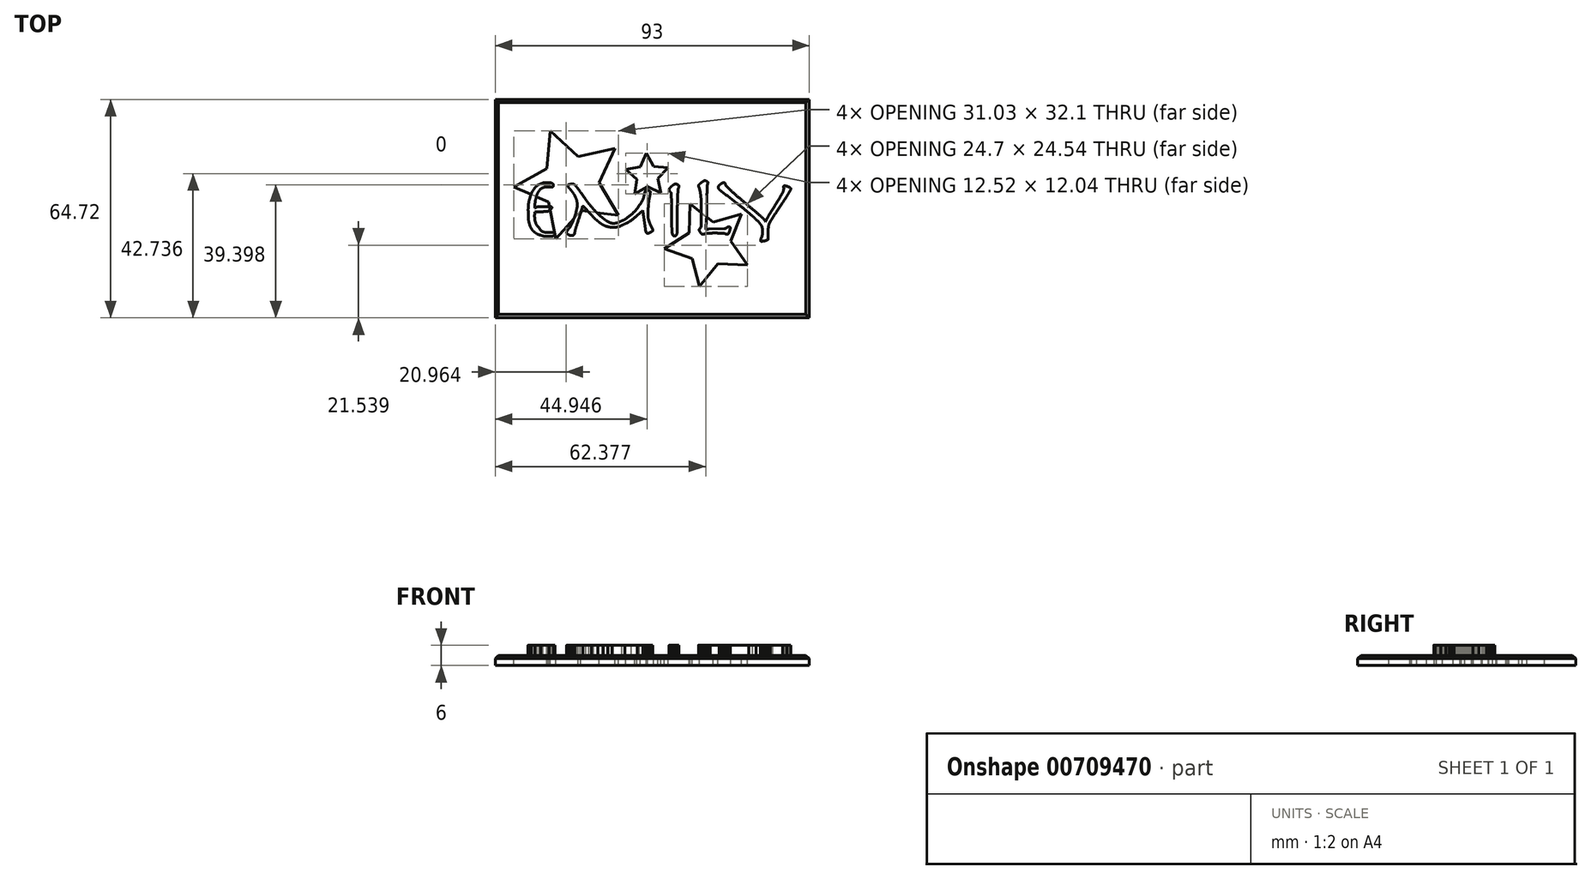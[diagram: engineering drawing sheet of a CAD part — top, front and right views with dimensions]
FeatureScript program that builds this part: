
annotation { "Feature Type Name" : "Feature", "Feature Type Description" : "" }
export const myFeature = defineFeature(function(context is Context, id is Id, definition is map)
    precondition{}
    {
        {
            var Q0;
            Q0=qCreatedBy(makeId("Top.planeOp"),FACE);
            var sketch = newSketch(context, id + "F0", { "sketchPlane" : qUnion([Q0])});
            skLineSegment(sketch, "E0", {"start": v(28.23, -16.77) * mm, "end": v(19.44, -16.28) * mm});
            skLineSegment(sketch, "E1", {"start": v(19.44, -16.28) * mm, "end": v(14.05, -23.1) * mm});
            skLineSegment(sketch, "E2", {"start": v(14.05, -23.1) * mm, "end": v(11.8, -14.75) * mm});
            skLineSegment(sketch, "E3", {"start": v(11.8, -14.75) * mm, "end": v(3.53, -11.83) * mm});
            skLineSegment(sketch, "E4", {"start": v(3.53, -11.83) * mm, "end": v(10.93, -7.17) * mm});
            skLineSegment(sketch, "E5", {"start": v(10.93, -7.17) * mm, "end": v(11.2, 1.45) * mm});
            skLineSegment(sketch, "E6", {"start": v(11.2, 1.45) * mm, "end": v(18.02, -4) * mm});
            skLineSegment(sketch, "E7", {"start": v(18.02, -4) * mm, "end": v(26.47, -1.6) * mm});
            skLineSegment(sketch, "E8", {"start": v(26.47, -1.6) * mm, "end": v(23.28, -9.64) * mm});
            skLineSegment(sketch, "E9", {"start": v(23.28, -9.64) * mm, "end": v(28.23, -16.77) * mm});
            skFitSpline(sketch, "E10", {"points": [v(-33.66, 0.52) * mm, v(-33.91, 0.52) * mm, v(-34.13, 0.48) * mm, v(-34.32, 0.4) * mm]});
            skFitSpline(sketch, "E11", {"points": [v(-34.32, 0.4) * mm, v(-34.5, 0.33) * mm, v(-34.67, 0.23) * mm, v(-34.8, 0.12) * mm]});
            skFitSpline(sketch, "E12", {"points": [v(-34.8, 0.12) * mm, v(-34.73, 1.39) * mm, v(-34.6, 2.43) * mm, v(-34.37, 3.24) * mm]});
            skFitSpline(sketch, "E13", {"points": [v(-34.37, 3.24) * mm, v(-34.15, 4.05) * mm, v(-33.89, 4.69) * mm, v(-33.58, 5.15) * mm]});
            skFitSpline(sketch, "E14", {"points": [v(-33.58, 5.15) * mm, v(-33.26, 5.62) * mm, v(-32.91, 5.94) * mm, v(-32.54, 6.11) * mm]});
            skFitSpline(sketch, "E15", {"points": [v(-32.54, 6.11) * mm, v(-32.15, 6.28) * mm, v(-31.75, 6.36) * mm, v(-31.35, 6.36) * mm]});
            skLineSegment(sketch, "E16", {"start": v(-30.23, 0.52) * mm, "end": v(-33.66, 0.52) * mm});
            skLineSegment(sketch, "E17", {"start": v(-33.66, 0.52) * mm, "end": v(-30.23, 0.52) * mm});
            skFitSpline(sketch, "E18", {"points": [v(-29.85, 6.36) * mm, v(-29.53, 6.36) * mm, v(-29.37, 6.55) * mm, v(-29.37, 6.92) * mm]});
            skFitSpline(sketch, "E19", {"points": [v(-29.37, 6.92) * mm, v(-29.37, 7.21) * mm, v(-29.5, 7.4) * mm, v(-29.75, 7.5) * mm]});
            skFitSpline(sketch, "E20", {"points": [v(-29.75, 7.5) * mm, v(-30, 7.63) * mm, v(-30.48, 7.69) * mm, v(-31.2, 7.69) * mm]});
            skFitSpline(sketch, "E21", {"points": [v(-31.2, 7.69) * mm, v(-31.9, 7.69) * mm, v(-32.6, 7.53) * mm, v(-33.28, 7.23) * mm]});
            skFitSpline(sketch, "E22", {"points": [v(-33.28, 7.23) * mm, v(-33.94, 6.94) * mm, v(-34.52, 6.44) * mm, v(-35.03, 5.73) * mm]});
            skFitSpline(sketch, "E23", {"points": [v(-35.03, 5.73) * mm, v(-35.54, 5.04) * mm, v(-35.95, 4.11) * mm, v(-36.28, 2.96) * mm]});
            skFitSpline(sketch, "E24", {"points": [v(-36.28, 2.96) * mm, v(-36.58, 1.83) * mm, v(-36.73, 0.41) * mm, v(-36.73, -1.28) * mm]});
            skFitSpline(sketch, "E25", {"points": [v(-36.73, -1.28) * mm, v(-36.73, -1.75) * mm, v(-36.72, -2.25) * mm, v(-36.68, -2.78) * mm]});
            skFitSpline(sketch, "E26", {"points": [v(-36.68, -2.78) * mm, v(-36.65, -3.3) * mm, v(-36.56, -3.83) * mm, v(-36.43, -4.35) * mm]});
            skFitSpline(sketch, "E27", {"points": [v(-36.43, -4.35) * mm, v(-36.3, -4.86) * mm, v(-36.1, -5.35) * mm, v(-35.84, -5.83) * mm]});
            skFitSpline(sketch, "E28", {"points": [v(-35.84, -5.83) * mm, v(-35.57, -6.28) * mm, v(-35.2, -6.7) * mm, v(-34.75, -7.05) * mm]});
            skFitSpline(sketch, "E29", {"points": [v(-34.75, -7.05) * mm, v(-34.3, -7.4) * mm, v(-33.73, -7.68) * mm, v(-33.05, -7.88) * mm]});
            skFitSpline(sketch, "E30", {"points": [v(-33.05, -7.88) * mm, v(-32.37, -8.1) * mm, v(-31.55, -8.21) * mm, v(-30.59, -8.21) * mm]});
            skFitSpline(sketch, "E31", {"points": [v(-30.59, -8.21) * mm, v(-29.94, -8.21) * mm, v(-29.5, -8.15) * mm, v(-29.24, -8.01) * mm]});
            skFitSpline(sketch, "E32", {"points": [v(-29.24, -8.01) * mm, v(-28.99, -7.88) * mm, v(-28.86, -7.74) * mm, v(-28.86, -7.6) * mm]});
            skFitSpline(sketch, "E33", {"points": [v(-28.86, -7.6) * mm, v(-28.86, -7.39) * mm, v(-28.93, -7.24) * mm, v(-29.06, -7.17) * mm]});
            skFitSpline(sketch, "E34", {"points": [v(-29.06, -7.17) * mm, v(-29.18, -7.1) * mm, v(-29.43, -7.07) * mm, v(-29.8, -7.07) * mm]});
            skFitSpline(sketch, "E35", {"points": [v(-29.8, -7.07) * mm, v(-31.54, -7.07) * mm, v(-32.81, -6.56) * mm, v(-33.6, -5.55) * mm]});
            skFitSpline(sketch, "E36", {"points": [v(-33.6, -5.55) * mm, v(-34.4, -4.52) * mm, v(-34.8, -2.98) * mm, v(-34.8, -0.95) * mm]});
            skFitSpline(sketch, "E37", {"points": [v(-34.8, -0.95) * mm, v(-34.3, -0.93) * mm, v(-33.72, -0.93) * mm, v(-33.07, -0.93) * mm]});
            skFitSpline(sketch, "E38", {"points": [v(-33.07, -0.93) * mm, v(-32.41, -0.9) * mm, v(-31.7, -0.87) * mm, v(-30.94, -0.8) * mm]});
            skFitSpline(sketch, "E39", {"points": [v(-30.94, -0.8) * mm, v(-30.86, -0.8) * mm, v(-30.75, -0.76) * mm, v(-30.64, -0.67) * mm]});
            skFitSpline(sketch, "E40", {"points": [v(-30.64, -0.67) * mm, v(-30.5, -0.59) * mm, v(-30.37, -0.48) * mm, v(-30.23, -0.37) * mm]});
            skFitSpline(sketch, "E41", {"points": [v(-30.23, -0.37) * mm, v(-30.1, -0.25) * mm, v(-29.98, -0.14) * mm, v(-29.9, -0.04) * mm]});
            skFitSpline(sketch, "E42", {"points": [v(-29.9, -0.04) * mm, v(-29.8, 0.08) * mm, v(-29.75, 0.17) * mm, v(-29.75, 0.22) * mm]});
            skFitSpline(sketch, "E43", {"points": [v(-29.75, 0.22) * mm, v(-29.75, 0.42) * mm, v(-29.9, 0.52) * mm, v(-30.23, 0.52) * mm]});
            skLineSegment(sketch, "E44", {"start": v(-31.35, 6.36) * mm, "end": v(-29.85, 6.36) * mm});
            skLineSegment(sketch, "E45", {"start": v(-29.85, 6.36) * mm, "end": v(-31.35, 6.36) * mm});
            skFitSpline(sketch, "E46", {"points": [v(-18, -1.9) * mm, v(-17.32, -2.62) * mm, v(-16.7, -3.22) * mm, v(-16.15, -3.7) * mm]});
            skFitSpline(sketch, "E47", {"points": [v(-16.15, -3.7) * mm, v(-15.59, -4.15) * mm, v(-15.07, -4.52) * mm, v(-14.6, -4.79) * mm]});
            skFitSpline(sketch, "E48", {"points": [v(-14.6, -4.79) * mm, v(-14.1, -5.06) * mm, v(-13.64, -5.24) * mm, v(-13.2, -5.34) * mm]});
            skFitSpline(sketch, "E49", {"points": [v(-13.2, -5.34) * mm, v(-12.76, -5.45) * mm, v(-12.31, -5.5) * mm, v(-11.85, -5.5) * mm]});
            skFitSpline(sketch, "E50", {"points": [v(-11.85, -5.5) * mm, v(-10.67, -5.5) * mm, v(-9.42, -5.18) * mm, v(-8.12, -4.53) * mm]});
            skFitSpline(sketch, "E51", {"points": [v(-8.12, -4.53) * mm, v(-6.82, -3.89) * mm, v(-5.57, -3.03) * mm, v(-4.39, -1.97) * mm]});
            skLineSegment(sketch, "E52", {"start": v(-20.57, 0.83) * mm, "end": v(-18, -1.9) * mm});
            skLineSegment(sketch, "E53", {"start": v(-18, -1.9) * mm, "end": v(-20.57, 0.83) * mm});
            skFitSpline(sketch, "E54", {"points": [v(-2.81, -0.54) * mm, v(-2.78, -0.73) * mm, v(-2.74, -1.04) * mm, v(-2.68, -1.46) * mm]});
            skFitSpline(sketch, "E55", {"points": [v(-2.68, -1.46) * mm, v(-2.62, -1.86) * mm, v(-2.55, -2.32) * mm, v(-2.48, -2.83) * mm]});
            skFitSpline(sketch, "E56", {"points": [v(-2.48, -2.83) * mm, v(-2.4, -3.34) * mm, v(-2.32, -3.85) * mm, v(-2.25, -4.38) * mm]});
            skFitSpline(sketch, "E57", {"points": [v(-2.25, -4.38) * mm, v(-2.17, -4.9) * mm, v(-2.1, -5.37) * mm, v(-2.05, -5.78) * mm]});
            skFitSpline(sketch, "E58", {"points": [v(-2.05, -5.78) * mm, v(-2, -6.25) * mm, v(-1.92, -6.62) * mm, v(-1.82, -6.9) * mm]});
            skFitSpline(sketch, "E59", {"points": [v(-1.82, -6.9) * mm, v(-1.7, -7.17) * mm, v(-1.54, -7.3) * mm, v(-1.34, -7.3) * mm]});
            skFitSpline(sketch, "E60", {"points": [v(-1.34, -7.3) * mm, v(-1.24, -7.3) * mm, v(-1.1, -7.28) * mm, v(-0.93, -7.22) * mm]});
            skFitSpline(sketch, "E61", {"points": [v(-0.93, -7.22) * mm, v(-0.76, -7.16) * mm, v(-0.6, -7.08) * mm, v(-0.45, -7) * mm]});
            skFitSpline(sketch, "E62", {"points": [v(-0.45, -7) * mm, v(-0.28, -6.91) * mm, v(-0.14, -6.83) * mm, v(-0.02, -6.74) * mm]});
            skFitSpline(sketch, "E63", {"points": [v(-0.02, -6.74) * mm, v(0.1, -6.64) * mm, v(0.16, -6.56) * mm, v(0.16, -6.49) * mm]});
            skFitSpline(sketch, "E64", {"points": [v(0.16, -6.49) * mm, v(0.16, -6.3) * mm, v(0.08, -6.06) * mm, v(-0.07, -5.78) * mm]});
            skFitSpline(sketch, "E65", {"points": [v(-0.07, -5.78) * mm, v(-0.2, -5.49) * mm, v(-0.36, -5.15) * mm, v(-0.55, -4.76) * mm]});
            skFitSpline(sketch, "E66", {"points": [v(-0.55, -4.76) * mm, v(-0.72, -4.37) * mm, v(-0.88, -3.93) * mm, v(-1.03, -3.44) * mm]});
            skFitSpline(sketch, "E67", {"points": [v(-1.03, -3.44) * mm, v(-1.17, -2.93) * mm, v(-1.24, -2.37) * mm, v(-1.24, -1.76) * mm]});
            skFitSpline(sketch, "E68", {"points": [v(-1.24, -1.76) * mm, v(-1.24, -0.83) * mm, v(-1.2, 0.01) * mm, v(-1.14, 0.78) * mm]});
            skFitSpline(sketch, "E69", {"points": [v(-1.14, 0.78) * mm, v(-1.07, 1.54) * mm, v(-1, 2.2) * mm, v(-0.9, 2.76) * mm]});
            skFitSpline(sketch, "E70", {"points": [v(-0.9, 2.76) * mm, v(-0.8, 3.32) * mm, v(-0.72, 3.77) * mm, v(-0.65, 4.13) * mm]});
            skFitSpline(sketch, "E71", {"points": [v(-0.65, 4.13) * mm, v(-0.58, 4.5) * mm, v(-0.55, 4.76) * mm, v(-0.55, 4.9) * mm]});
            skFitSpline(sketch, "E72", {"points": [v(-0.55, 4.9) * mm, v(-0.55, 5) * mm, v(-0.6, 5.08) * mm, v(-0.7, 5.15) * mm]});
            skFitSpline(sketch, "E73", {"points": [v(-0.7, 5.15) * mm, v(-0.79, 5.23) * mm, v(-0.9, 5.3) * mm, v(-1.03, 5.35) * mm]});
            skFitSpline(sketch, "E74", {"points": [v(-1.03, 5.35) * mm, v(-1.15, 5.42) * mm, v(-1.28, 5.46) * mm, v(-1.41, 5.48) * mm]});
            skFitSpline(sketch, "E75", {"points": [v(-1.41, 5.48) * mm, v(-1.53, 5.5) * mm, v(-1.63, 5.53) * mm, v(-1.7, 5.53) * mm]});
            skFitSpline(sketch, "E76", {"points": [v(-1.7, 5.53) * mm, v(-1.8, 5.53) * mm, v(-1.9, 5.44) * mm, v(-2, 5.27) * mm]});
            skFitSpline(sketch, "E77", {"points": [v(-2, 5.27) * mm, v(-2.08, 5.1) * mm, v(-2.18, 4.8) * mm, v(-2.28, 4.38) * mm]});
            skFitSpline(sketch, "E78", {"points": [v(-2.28, 4.38) * mm, v(-2.58, 3.13) * mm, v(-3.12, 1.97) * mm, v(-3.88, 0.9) * mm]});
            skFitSpline(sketch, "E79", {"points": [v(-3.88, 0.9) * mm, v(-4.62, -0.16) * mm, v(-5.45, -1.09) * mm, v(-6.37, -1.86) * mm]});
            skFitSpline(sketch, "E80", {"points": [v(-6.37, -1.86) * mm, v(-7.28, -2.63) * mm, v(-8.21, -3.23) * mm, v(-9.16, -3.67) * mm]});
            skFitSpline(sketch, "E81", {"points": [v(-9.16, -3.67) * mm, v(-10.1, -4.1) * mm, v(-10.9, -4.33) * mm, v(-11.6, -4.33) * mm]});
            skFitSpline(sketch, "E82", {"points": [v(-11.6, -4.33) * mm, v(-11.97, -4.33) * mm, v(-12.4, -4.21) * mm, v(-12.87, -3.97) * mm]});
            skFitSpline(sketch, "E83", {"points": [v(-12.87, -3.97) * mm, v(-13.33, -3.74) * mm, v(-13.82, -3.42) * mm, v(-14.34, -3.03) * mm]});
            skFitSpline(sketch, "E84", {"points": [v(-14.34, -3.03) * mm, v(-14.85, -2.63) * mm, v(-15.37, -2.18) * mm, v(-15.9, -1.69) * mm]});
            skFitSpline(sketch, "E85", {"points": [v(-15.9, -1.69) * mm, v(-16.42, -1.18) * mm, v(-16.93, -0.66) * mm, v(-17.42, -0.14) * mm]});
            skFitSpline(sketch, "E86", {"points": [v(-17.42, -0.14) * mm, v(-17.9, 0.4) * mm, v(-18.34, 0.93) * mm, v(-18.76, 1.44) * mm]});
            skFitSpline(sketch, "E87", {"points": [v(-18.76, 1.44) * mm, v(-19.17, 1.96) * mm, v(-19.52, 2.43) * mm, v(-19.8, 2.83) * mm]});
            skFitSpline(sketch, "E88", {"points": [v(-19.8, 2.83) * mm, v(-20.46, 3.8) * mm, v(-21.01, 4.58) * mm, v(-21.46, 5.17) * mm]});
            skFitSpline(sketch, "E89", {"points": [v(-21.46, 5.17) * mm, v(-21.88, 5.76) * mm, v(-22.23, 6.21) * mm, v(-22.5, 6.52) * mm]});
            skFitSpline(sketch, "E90", {"points": [v(-22.5, 6.52) * mm, v(-22.75, 6.84) * mm, v(-22.95, 7.05) * mm, v(-23.1, 7.15) * mm]});
            skFitSpline(sketch, "E91", {"points": [v(-23.1, 7.15) * mm, v(-23.26, 7.25) * mm, v(-23.4, 7.3) * mm, v(-23.51, 7.3) * mm]});
            skFitSpline(sketch, "E92", {"points": [v(-23.51, 7.3) * mm, v(-23.63, 7.3) * mm, v(-23.77, 7.3) * mm, v(-23.94, 7.28) * mm]});
            skFitSpline(sketch, "E93", {"points": [v(-23.94, 7.28) * mm, v(-24.1, 7.26) * mm, v(-24.25, 7.24) * mm, v(-24.4, 7.2) * mm]});
            skFitSpline(sketch, "E94", {"points": [v(-24.4, 7.2) * mm, v(-24.55, 7.17) * mm, v(-24.69, 7.13) * mm, v(-24.8, 7.08) * mm]});
            skFitSpline(sketch, "E95", {"points": [v(-24.8, 7.08) * mm, v(-24.9, 7.03) * mm, v(-24.96, 6.96) * mm, v(-24.96, 6.87) * mm]});
            skFitSpline(sketch, "E96", {"points": [v(-24.96, 6.87) * mm, v(-24.96, 6.65) * mm, v(-24.82, 6.37) * mm, v(-24.55, 6.03) * mm]});
            skFitSpline(sketch, "E97", {"points": [v(-24.55, 6.03) * mm, v(-24.27, 5.71) * mm, v(-23.95, 5.31) * mm, v(-23.61, 4.84) * mm]});
            skFitSpline(sketch, "E98", {"points": [v(-23.61, 4.84) * mm, v(-23.26, 4.38) * mm, v(-22.95, 3.83) * mm, v(-22.67, 3.19) * mm]});
            skFitSpline(sketch, "E99", {"points": [v(-22.67, 3.19) * mm, v(-22.39, 2.55) * mm, v(-22.24, 1.8) * mm, v(-22.24, 0.93) * mm]});
            skFitSpline(sketch, "E100", {"points": [v(-22.24, 0.93) * mm, v(-22.24, 0.5) * mm, v(-22.33, -0.04) * mm, v(-22.5, -0.72) * mm]});
            skFitSpline(sketch, "E101", {"points": [v(-22.5, -0.72) * mm, v(-22.65, -1.38) * mm, v(-22.85, -2.06) * mm, v(-23.1, -2.75) * mm]});
            skFitSpline(sketch, "E102", {"points": [v(-23.1, -2.75) * mm, v(-23.36, -3.45) * mm, v(-23.64, -4.1) * mm, v(-23.94, -4.74) * mm]});
            skFitSpline(sketch, "E103", {"points": [v(-23.94, -4.74) * mm, v(-24.25, -5.34) * mm, v(-24.54, -5.8) * mm, v(-24.8, -6.1) * mm]});
            skFitSpline(sketch, "E104", {"points": [v(-24.8, -6.1) * mm, v(-25.04, -6.38) * mm, v(-25.2, -6.58) * mm, v(-25.27, -6.72) * mm]});
            skFitSpline(sketch, "E105", {"points": [v(-25.27, -6.72) * mm, v(-25.33, -6.85) * mm, v(-25.37, -6.97) * mm, v(-25.37, -7.07) * mm]});
            skFitSpline(sketch, "E106", {"points": [v(-25.37, -7.07) * mm, v(-25.37, -7.14) * mm, v(-25.33, -7.22) * mm, v(-25.27, -7.33) * mm]});
            skFitSpline(sketch, "E107", {"points": [v(-25.27, -7.33) * mm, v(-25.18, -7.43) * mm, v(-25.08, -7.52) * mm, v(-24.96, -7.6) * mm]});
            skFitSpline(sketch, "E108", {"points": [v(-24.96, -7.6) * mm, v(-24.84, -7.7) * mm, v(-24.71, -7.8) * mm, v(-24.58, -7.86) * mm]});
            skFitSpline(sketch, "E109", {"points": [v(-24.58, -7.86) * mm, v(-24.44, -7.93) * mm, v(-24.32, -7.96) * mm, v(-24.2, -7.96) * mm]});
            skFitSpline(sketch, "E110", {"points": [v(-24.2, -7.96) * mm, v(-23.96, -7.96) * mm, v(-23.77, -7.95) * mm, v(-23.64, -7.94) * mm]});
            skFitSpline(sketch, "E111", {"points": [v(-23.64, -7.94) * mm, v(-23.49, -7.92) * mm, v(-23.37, -7.88) * mm, v(-23.28, -7.83) * mm]});
            skFitSpline(sketch, "E112", {"points": [v(-23.28, -7.83) * mm, v(-23.2, -7.8) * mm, v(-23.14, -7.74) * mm, v(-23.1, -7.66) * mm]});
            skFitSpline(sketch, "E113", {"points": [v(-23.1, -7.66) * mm, v(-23.07, -7.57) * mm, v(-23.04, -7.46) * mm, v(-23, -7.33) * mm]});
            skFitSpline(sketch, "E114", {"points": [v(-23, -7.33) * mm, v(-22.87, -6.67) * mm, v(-22.57, -5.62) * mm, v(-22.12, -4.2) * mm]});
            skFitSpline(sketch, "E115", {"points": [v(-22.12, -4.2) * mm, v(-21.64, -2.78) * mm, v(-21.12, -1.1) * mm, v(-20.57, 0.83) * mm]});
            skLineSegment(sketch, "E116", {"start": v(-4.39, -1.97) * mm, "end": v(-2.81, -0.54) * mm});
            skLineSegment(sketch, "E117", {"start": v(-2.81, -0.54) * mm, "end": v(-4.39, -1.97) * mm});
            skFitSpline(sketch, "E118", {"points": [v(5.75, 0.24) * mm, v(5.75, -1.1) * mm, v(5.75, -2.24) * mm, v(5.75, -3.19) * mm]});
            skFitSpline(sketch, "E119", {"points": [v(5.75, -3.19) * mm, v(5.77, -4.12) * mm, v(5.78, -4.9) * mm, v(5.8, -5.52) * mm]});
            skFitSpline(sketch, "E120", {"points": [v(5.8, -5.52) * mm, v(5.82, -6.13) * mm, v(5.84, -6.61) * mm, v(5.88, -6.97) * mm]});
            skFitSpline(sketch, "E121", {"points": [v(5.88, -6.97) * mm, v(5.93, -7.3) * mm, v(5.99, -7.56) * mm, v(6.05, -7.73) * mm]});
            skFitSpline(sketch, "E122", {"points": [v(6.05, -7.73) * mm, v(6.12, -7.9) * mm, v(6.2, -8) * mm, v(6.28, -8.04) * mm]});
            skFitSpline(sketch, "E123", {"points": [v(6.28, -8.04) * mm, v(6.38, -8.09) * mm, v(6.5, -8.11) * mm, v(6.61, -8.11) * mm]});
            skFitSpline(sketch, "E124", {"points": [v(6.61, -8.11) * mm, v(6.9, -8.11) * mm, v(7.1, -7.94) * mm, v(7.22, -7.6) * mm]});
            skFitSpline(sketch, "E125", {"points": [v(7.22, -7.6) * mm, v(7.36, -7.28) * mm, v(7.43, -6.61) * mm, v(7.43, -5.6) * mm]});
            skFitSpline(sketch, "E126", {"points": [v(7.43, -5.6) * mm, v(7.43, -2.55) * mm, v(7.44, -0.15) * mm, v(7.48, 1.59) * mm]});
            skFitSpline(sketch, "E127", {"points": [v(7.48, 1.59) * mm, v(7.53, 3.35) * mm, v(7.59, 4.6) * mm, v(7.65, 5.35) * mm]});
            skFitSpline(sketch, "E128", {"points": [v(7.65, 5.35) * mm, v(7.67, 5.64) * mm, v(7.71, 5.88) * mm, v(7.78, 6.09) * mm]});
            skFitSpline(sketch, "E129", {"points": [v(7.78, 6.09) * mm, v(7.87, 6.3) * mm, v(7.9, 6.52) * mm, v(7.9, 6.72) * mm]});
            skFitSpline(sketch, "E130", {"points": [v(7.9, 6.72) * mm, v(7.9, 6.82) * mm, v(7.79, 6.94) * mm, v(7.55, 7.08) * mm]});
            skFitSpline(sketch, "E131", {"points": [v(7.55, 7.08) * mm, v(7.32, 7.23) * mm, v(7.1, 7.3) * mm, v(6.92, 7.3) * mm]});
            skFitSpline(sketch, "E132", {"points": [v(6.92, 7.3) * mm, v(6.8, 7.3) * mm, v(6.63, 7.24) * mm, v(6.4, 7.1) * mm]});
            skFitSpline(sketch, "E133", {"points": [v(6.4, 7.1) * mm, v(6.2, 6.98) * mm, v(6, 6.84) * mm, v(5.8, 6.67) * mm]});
            skFitSpline(sketch, "E134", {"points": [v(5.8, 6.67) * mm, v(5.6, 6.5) * mm, v(5.42, 6.32) * mm, v(5.27, 6.14) * mm]});
            skFitSpline(sketch, "E135", {"points": [v(5.27, 6.14) * mm, v(5.11, 5.95) * mm, v(5.04, 5.8) * mm, v(5.04, 5.7) * mm]});
            skFitSpline(sketch, "E136", {"points": [v(5.04, 5.7) * mm, v(5.04, 5.57) * mm, v(5.06, 5.42) * mm, v(5.11, 5.27) * mm]});
            skFitSpline(sketch, "E137", {"points": [v(5.11, 5.27) * mm, v(5.18, 5.14) * mm, v(5.3, 4.98) * mm, v(5.47, 4.79) * mm]});
            skFitSpline(sketch, "E138", {"points": [v(5.47, 4.79) * mm, v(5.57, 4.67) * mm, v(5.63, 4.53) * mm, v(5.65, 4.36) * mm]});
            skFitSpline(sketch, "E139", {"points": [v(5.65, 4.36) * mm, v(5.66, 4.2) * mm, v(5.67, 4.01) * mm, v(5.67, 3.77) * mm]});
            skFitSpline(sketch, "E140", {"points": [v(5.67, 3.77) * mm, v(5.67, 3.33) * mm, v(5.68, 2.86) * mm, v(5.7, 2.35) * mm]});
            skFitSpline(sketch, "E141", {"points": [v(5.7, 2.35) * mm, v(5.73, 1.84) * mm, v(5.75, 1.14) * mm, v(5.75, 0.24) * mm]});
            skFitSpline(sketch, "E142", {"points": [v(16.75, -6.08) * mm, v(16.63, -6.08) * mm, v(16.52, -6.1) * mm, v(16.42, -6.13) * mm]});
            skFitSpline(sketch, "E143", {"points": [v(16.42, -6.13) * mm, v(16.33, -6.17) * mm, v(16.25, -6.18) * mm, v(16.16, -6.18) * mm]});
            skFitSpline(sketch, "E144", {"points": [v(16.16, -6.18) * mm, v(15.96, -6.18) * mm, v(15.86, -6.12) * mm, v(15.86, -5.98) * mm]});
            skFitSpline(sketch, "E145", {"points": [v(15.86, -5.98) * mm, v(15.86, -5.83) * mm, v(15.88, -5.57) * mm, v(15.9, -5.22) * mm]});
            skFitSpline(sketch, "E146", {"points": [v(15.9, -5.22) * mm, v(15.94, -4.86) * mm, v(15.98, -4.45) * mm, v(16.01, -3.97) * mm]});
            skFitSpline(sketch, "E147", {"points": [v(16.01, -3.97) * mm, v(16.04, -3.5) * mm, v(16.08, -3) * mm, v(16.11, -2.45) * mm]});
            skFitSpline(sketch, "E148", {"points": [v(16.11, -2.45) * mm, v(16.15, -1.9) * mm, v(16.16, -1.35) * mm, v(16.16, -0.82) * mm]});
            skFitSpline(sketch, "E149", {"points": [v(16.16, -0.82) * mm, v(16.16, -0.26) * mm, v(16.16, 0.22) * mm, v(16.14, 0.62) * mm]});
            skFitSpline(sketch, "E150", {"points": [v(16.14, 0.62) * mm, v(16.12, 1.05) * mm, v(16.11, 1.5) * mm, v(16.11, 1.97) * mm]});
            skFitSpline(sketch, "E151", {"points": [v(16.11, 1.97) * mm, v(16.11, 2.68) * mm, v(16.14, 3.4) * mm, v(16.19, 4.15) * mm]});
            skFitSpline(sketch, "E152", {"points": [v(16.19, 4.15) * mm, v(16.24, 4.9) * mm, v(16.27, 5.65) * mm, v(16.27, 6.42) * mm]});
            skFitSpline(sketch, "E153", {"points": [v(16.27, 6.42) * mm, v(16.27, 6.65) * mm, v(16.3, 6.88) * mm, v(16.37, 7.1) * mm]});
            skFitSpline(sketch, "E154", {"points": [v(16.37, 7.1) * mm, v(16.43, 7.32) * mm, v(16.47, 7.5) * mm, v(16.47, 7.66) * mm]});
            skFitSpline(sketch, "E155", {"points": [v(16.47, 7.66) * mm, v(16.47, 7.85) * mm, v(16.36, 8) * mm, v(16.14, 8.1) * mm]});
            skFitSpline(sketch, "E156", {"points": [v(16.14, 8.1) * mm, v(15.92, 8.21) * mm, v(15.73, 8.27) * mm, v(15.58, 8.27) * mm]});
            skFitSpline(sketch, "E157", {"points": [v(15.58, 8.27) * mm, v(15.5, 8.27) * mm, v(15.34, 8.21) * mm, v(15.12, 8.1) * mm]});
            skFitSpline(sketch, "E158", {"points": [v(15.12, 8.1) * mm, v(14.92, 7.97) * mm, v(14.7, 7.83) * mm, v(14.49, 7.66) * mm]});
            skFitSpline(sketch, "E159", {"points": [v(14.49, 7.66) * mm, v(14.28, 7.5) * mm, v(14.1, 7.35) * mm, v(13.93, 7.18) * mm]});
            skFitSpline(sketch, "E160", {"points": [v(13.93, 7.18) * mm, v(13.78, 7) * mm, v(13.7, 6.88) * mm, v(13.7, 6.8) * mm]});
            skFitSpline(sketch, "E161", {"points": [v(13.7, 6.8) * mm, v(13.7, 6.7) * mm, v(13.74, 6.56) * mm, v(13.83, 6.4) * mm]});
            skFitSpline(sketch, "E162", {"points": [v(13.83, 6.4) * mm, v(13.91, 6.24) * mm, v(14, 5.95) * mm, v(14.08, 5.53) * mm]});
            skFitSpline(sketch, "E163", {"points": [v(14.08, 5.53) * mm, v(14.18, 5.12) * mm, v(14.28, 4.54) * mm, v(14.36, 3.8) * mm]});
            skFitSpline(sketch, "E164", {"points": [v(14.36, 3.8) * mm, v(14.44, 3.07) * mm, v(14.49, 2.09) * mm, v(14.49, 0.85) * mm]});
            skLineSegment(sketch, "E165", {"start": v(21.35, -5.9) * mm, "end": v(16.75, -6.08) * mm});
            skLineSegment(sketch, "E166", {"start": v(16.75, -6.08) * mm, "end": v(21.35, -5.9) * mm});
            skFitSpline(sketch, "E167", {"points": [v(14.49, -2.73) * mm, v(14.49, -3.25) * mm, v(14.48, -3.71) * mm, v(14.46, -4.1) * mm]});
            skFitSpline(sketch, "E168", {"points": [v(14.46, -4.1) * mm, v(14.46, -4.49) * mm, v(14.45, -4.82) * mm, v(14.44, -5.1) * mm]});
            skFitSpline(sketch, "E169", {"points": [v(14.44, -5.1) * mm, v(14.44, -5.41) * mm, v(14.35, -5.67) * mm, v(14.18, -5.85) * mm]});
            skFitSpline(sketch, "E170", {"points": [v(14.18, -5.85) * mm, v(14.01, -6.02) * mm, v(13.93, -6.17) * mm, v(13.93, -6.3) * mm]});
            skFitSpline(sketch, "E171", {"points": [v(13.93, -6.3) * mm, v(13.93, -6.36) * mm, v(13.95, -6.46) * mm, v(14, -6.61) * mm]});
            skFitSpline(sketch, "E172", {"points": [v(14, -6.61) * mm, v(14.07, -6.75) * mm, v(14.16, -6.9) * mm, v(14.26, -7.05) * mm]});
            skFitSpline(sketch, "E173", {"points": [v(14.26, -7.05) * mm, v(14.36, -7.18) * mm, v(14.46, -7.3) * mm, v(14.56, -7.43) * mm]});
            skFitSpline(sketch, "E174", {"points": [v(14.56, -7.43) * mm, v(14.68, -7.55) * mm, v(14.8, -7.6) * mm, v(14.9, -7.6) * mm]});
            skFitSpline(sketch, "E175", {"points": [v(14.9, -7.6) * mm, v(15.2, -7.6) * mm, v(15.46, -7.55) * mm, v(15.68, -7.43) * mm]});
            skFitSpline(sketch, "E176", {"points": [v(15.68, -7.43) * mm, v(15.75, -7.4) * mm, v(15.82, -7.37) * mm, v(15.9, -7.35) * mm]});
            skFitSpline(sketch, "E177", {"points": [v(15.9, -7.35) * mm, v(16.01, -7.32) * mm, v(16.16, -7.3) * mm, v(16.37, -7.3) * mm]});
            skFitSpline(sketch, "E178", {"points": [v(16.37, -7.3) * mm, v(16.57, -7.28) * mm, v(16.84, -7.28) * mm, v(17.18, -7.28) * mm]});
            skFitSpline(sketch, "E179", {"points": [v(17.18, -7.28) * mm, v(17.54, -7.26) * mm, v(18, -7.25) * mm, v(18.58, -7.25) * mm]});
            skFitSpline(sketch, "E180", {"points": [v(18.58, -7.25) * mm, v(19.12, -7.25) * mm, v(19.56, -7.26) * mm, v(19.9, -7.28) * mm]});
            skFitSpline(sketch, "E181", {"points": [v(19.9, -7.28) * mm, v(20.25, -7.28) * mm, v(20.53, -7.28) * mm, v(20.74, -7.3) * mm]});
            skFitSpline(sketch, "E182", {"points": [v(20.74, -7.3) * mm, v(20.94, -7.3) * mm, v(21.08, -7.3) * mm, v(21.17, -7.33) * mm]});
            skFitSpline(sketch, "E183", {"points": [v(21.17, -7.33) * mm, v(21.25, -7.33) * mm, v(21.31, -7.33) * mm, v(21.35, -7.35) * mm]});
            skFitSpline(sketch, "E184", {"points": [v(21.35, -7.35) * mm, v(21.6, -7.44) * mm, v(21.79, -7.5) * mm, v(21.9, -7.55) * mm]});
            skFitSpline(sketch, "E185", {"points": [v(21.9, -7.55) * mm, v(22.04, -7.59) * mm, v(22.18, -7.6) * mm, v(22.34, -7.6) * mm]});
            skFitSpline(sketch, "E186", {"points": [v(22.34, -7.6) * mm, v(22.44, -7.6) * mm, v(22.53, -7.52) * mm, v(22.62, -7.35) * mm]});
            skFitSpline(sketch, "E187", {"points": [v(22.62, -7.35) * mm, v(22.72, -7.17) * mm, v(22.8, -6.97) * mm, v(22.87, -6.77) * mm]});
            skFitSpline(sketch, "E188", {"points": [v(22.87, -6.77) * mm, v(22.95, -6.55) * mm, v(23.01, -6.34) * mm, v(23.05, -6.16) * mm]});
            skFitSpline(sketch, "E189", {"points": [v(23.05, -6.16) * mm, v(23.1, -5.95) * mm, v(23.12, -5.83) * mm, v(23.12, -5.78) * mm]});
            skFitSpline(sketch, "E190", {"points": [v(23.12, -5.78) * mm, v(23.12, -5.56) * mm, v(22.98, -5.45) * mm, v(22.7, -5.45) * mm]});
            skFitSpline(sketch, "E191", {"points": [v(22.7, -5.45) * mm, v(22.5, -5.45) * mm, v(22.3, -5.52) * mm, v(22.06, -5.67) * mm]});
            skFitSpline(sketch, "E192", {"points": [v(22.06, -5.67) * mm, v(21.82, -5.81) * mm, v(21.58, -5.89) * mm, v(21.35, -5.9) * mm]});
            skLineSegment(sketch, "E193", {"start": v(14.49, 0.85) * mm, "end": v(14.49, -2.73) * mm});
            skLineSegment(sketch, "E194", {"start": v(14.49, -2.73) * mm, "end": v(14.49, 0.85) * mm});
            skFitSpline(sketch, "E195", {"points": [v(38.97, 6) * mm, v(38.97, 5.82) * mm, v(38.92, 5.59) * mm, v(38.84, 5.3) * mm]});
            skFitSpline(sketch, "E196", {"points": [v(38.84, 5.3) * mm, v(38.77, 5.03) * mm, v(38.64, 4.73) * mm, v(38.46, 4.4) * mm]});
            skFitSpline(sketch, "E197", {"points": [v(38.46, 4.4) * mm, v(38.05, 3.7) * mm, v(37.61, 2.95) * mm, v(37.14, 2.17) * mm]});
            skFitSpline(sketch, "E198", {"points": [v(37.14, 2.17) * mm, v(36.66, 1.41) * mm, v(36.2, 0.66) * mm, v(35.74, -0.09) * mm]});
            skFitSpline(sketch, "E199", {"points": [v(35.74, -0.09) * mm, v(35.28, -0.82) * mm, v(34.86, -1.5) * mm, v(34.47, -2.17) * mm]});
            skFitSpline(sketch, "E200", {"points": [v(34.47, -2.17) * mm, v(34.08, -2.83) * mm, v(33.78, -3.4) * mm, v(33.56, -3.9) * mm]});
            skFitSpline(sketch, "E201", {"points": [v(33.56, -3.9) * mm, v(33.3, -3.44) * mm, v(32.84, -2.9) * mm, v(32.16, -2.3) * mm]});
            skFitSpline(sketch, "E202", {"points": [v(32.16, -2.3) * mm, v(31.48, -1.67) * mm, v(30.63, -0.94) * mm, v(29.62, -0.11) * mm]});
            skFitSpline(sketch, "E203", {"points": [v(29.62, -0.11) * mm, v(28.62, 0.73) * mm, v(27.48, 1.7) * mm, v(26.21, 2.78) * mm]});
            skFitSpline(sketch, "E204", {"points": [v(26.21, 2.78) * mm, v(24.94, 3.87) * mm, v(23.6, 5.1) * mm, v(22.15, 6.47) * mm]});
            skFitSpline(sketch, "E205", {"points": [v(22.15, 6.47) * mm, v(22.02, 6.58) * mm, v(21.91, 6.71) * mm, v(21.85, 6.85) * mm]});
            skFitSpline(sketch, "E206", {"points": [v(21.85, 6.85) * mm, v(21.78, 7) * mm, v(21.72, 7.14) * mm, v(21.67, 7.25) * mm]});
            skFitSpline(sketch, "E207", {"points": [v(21.67, 7.25) * mm, v(21.63, 7.37) * mm, v(21.6, 7.47) * mm, v(21.54, 7.56) * mm]});
            skFitSpline(sketch, "E208", {"points": [v(21.54, 7.56) * mm, v(21.5, 7.64) * mm, v(21.44, 7.69) * mm, v(21.34, 7.69) * mm]});
            skFitSpline(sketch, "E209", {"points": [v(21.34, 7.69) * mm, v(21.13, 7.69) * mm, v(20.92, 7.63) * mm, v(20.7, 7.53) * mm]});
            skFitSpline(sketch, "E210", {"points": [v(20.7, 7.53) * mm, v(20.5, 7.43) * mm, v(20.31, 7.31) * mm, v(20.14, 7.18) * mm]});
            skFitSpline(sketch, "E211", {"points": [v(20.14, 7.18) * mm, v(19.98, 7.04) * mm, v(19.83, 6.9) * mm, v(19.71, 6.77) * mm]});
            skFitSpline(sketch, "E212", {"points": [v(19.71, 6.77) * mm, v(19.61, 6.64) * mm, v(19.56, 6.53) * mm, v(19.56, 6.47) * mm]});
            skFitSpline(sketch, "E213", {"points": [v(19.56, 6.47) * mm, v(19.56, 6.28) * mm, v(19.59, 6.11) * mm, v(19.64, 5.96) * mm]});
            skFitSpline(sketch, "E214", {"points": [v(19.64, 5.96) * mm, v(19.7, 5.8) * mm, v(19.82, 5.66) * mm, v(20, 5.53) * mm]});
            skFitSpline(sketch, "E215", {"points": [v(20, 5.53) * mm, v(21.97, 3.99) * mm, v(23.67, 2.66) * mm, v(25.07, 1.56) * mm]});
            skFitSpline(sketch, "E216", {"points": [v(25.07, 1.56) * mm, v(26.48, 0.46) * mm, v(27.65, -0.48) * mm, v(28.58, -1.28) * mm]});
            skFitSpline(sketch, "E217", {"points": [v(28.58, -1.28) * mm, v(29.53, -2.06) * mm, v(30.27, -2.72) * mm, v(30.81, -3.26) * mm]});
            skFitSpline(sketch, "E218", {"points": [v(30.81, -3.26) * mm, v(31.37, -3.79) * mm, v(31.79, -4.24) * mm, v(32.06, -4.63) * mm]});
            skFitSpline(sketch, "E219", {"points": [v(32.06, -4.63) * mm, v(32.34, -5.02) * mm, v(32.52, -5.38) * mm, v(32.6, -5.7) * mm]});
            skFitSpline(sketch, "E220", {"points": [v(32.6, -5.7) * mm, v(32.68, -6) * mm, v(32.72, -6.33) * mm, v(32.72, -6.67) * mm]});
            skFitSpline(sketch, "E221", {"points": [v(32.72, -6.67) * mm, v(32.72, -7.1) * mm, v(32.68, -7.46) * mm, v(32.62, -7.73) * mm]});
            skFitSpline(sketch, "E222", {"points": [v(32.62, -7.73) * mm, v(32.56, -8) * mm, v(32.5, -8.23) * mm, v(32.41, -8.42) * mm]});
            skFitSpline(sketch, "E223", {"points": [v(32.41, -8.42) * mm, v(32.34, -8.6) * mm, v(32.28, -8.77) * mm, v(32.2, -8.93) * mm]});
            skFitSpline(sketch, "E224", {"points": [v(32.2, -8.93) * mm, v(32.14, -9.08) * mm, v(32.1, -9.25) * mm, v(32.1, -9.43) * mm]});
            skFitSpline(sketch, "E225", {"points": [v(32.1, -9.43) * mm, v(32.1, -9.62) * mm, v(32.18, -9.71) * mm, v(32.31, -9.71) * mm]});
            skFitSpline(sketch, "E226", {"points": [v(32.31, -9.71) * mm, v(32.36, -9.71) * mm, v(32.5, -9.7) * mm, v(32.72, -9.66) * mm]});
            skFitSpline(sketch, "E227", {"points": [v(32.72, -9.66) * mm, v(32.94, -9.65) * mm, v(33.17, -9.6) * mm, v(33.4, -9.54) * mm]});
            skFitSpline(sketch, "E228", {"points": [v(33.4, -9.54) * mm, v(33.66, -9.47) * mm, v(33.88, -9.4) * mm, v(34.06, -9.3) * mm]});
            skFitSpline(sketch, "E229", {"points": [v(34.06, -9.3) * mm, v(34.25, -9.22) * mm, v(34.34, -9.11) * mm, v(34.34, -8.98) * mm]});
            skFitSpline(sketch, "E230", {"points": [v(34.34, -8.98) * mm, v(34.34, -8.74) * mm, v(34.33, -8.5) * mm, v(34.32, -8.27) * mm]});
            skFitSpline(sketch, "E231", {"points": [v(34.32, -8.27) * mm, v(34.3, -8.05) * mm, v(34.3, -7.83) * mm, v(34.3, -7.63) * mm]});
            skFitSpline(sketch, "E232", {"points": [v(34.3, -7.63) * mm, v(34.3, -7.07) * mm, v(34.3, -6.59) * mm, v(34.34, -6.18) * mm]});
            skFitSpline(sketch, "E233", {"points": [v(34.34, -6.18) * mm, v(34.38, -5.78) * mm, v(34.42, -5.43) * mm, v(34.47, -5.14) * mm]});
            skFitSpline(sketch, "E234", {"points": [v(34.47, -5.14) * mm, v(34.54, -4.84) * mm, v(34.61, -4.58) * mm, v(34.7, -4.38) * mm]});
            skFitSpline(sketch, "E235", {"points": [v(34.7, -4.38) * mm, v(34.78, -4.16) * mm, v(34.88, -3.96) * mm, v(35, -3.8) * mm]});
            skFitSpline(sketch, "E236", {"points": [v(35, -3.8) * mm, v(35.3, -3.32) * mm, v(35.64, -2.77) * mm, v(36.04, -2.14) * mm]});
            skFitSpline(sketch, "E237", {"points": [v(36.04, -2.14) * mm, v(36.45, -1.52) * mm, v(36.87, -0.87) * mm, v(37.31, -0.21) * mm]});
            skFitSpline(sketch, "E238", {"points": [v(37.31, -0.21) * mm, v(37.77, 0.46) * mm, v(38.22, 1.13) * mm, v(38.66, 1.8) * mm]});
            skFitSpline(sketch, "E239", {"points": [v(38.66, 1.8) * mm, v(39.12, 2.47) * mm, v(39.52, 3.09) * mm, v(39.85, 3.65) * mm]});
            skFitSpline(sketch, "E240", {"points": [v(39.85, 3.65) * mm, v(40.21, 4.22) * mm, v(40.5, 4.7) * mm, v(40.72, 5.1) * mm]});
            skFitSpline(sketch, "E241", {"points": [v(40.72, 5.1) * mm, v(40.94, 5.5) * mm, v(41.05, 5.78) * mm, v(41.05, 5.93) * mm]});
            skFitSpline(sketch, "E242", {"points": [v(41.05, 5.93) * mm, v(41.05, 6.02) * mm, v(40.97, 6.11) * mm, v(40.82, 6.21) * mm]});
            skFitSpline(sketch, "E243", {"points": [v(40.82, 6.21) * mm, v(40.68, 6.31) * mm, v(40.52, 6.4) * mm, v(40.31, 6.47) * mm]});
            skFitSpline(sketch, "E244", {"points": [v(40.31, 6.47) * mm, v(40.1, 6.55) * mm, v(39.9, 6.62) * mm, v(39.7, 6.67) * mm]});
            skFitSpline(sketch, "E245", {"points": [v(39.7, 6.67) * mm, v(39.5, 6.72) * mm, v(39.35, 6.75) * mm, v(39.25, 6.75) * mm]});
            skFitSpline(sketch, "E246", {"points": [v(39.25, 6.75) * mm, v(39.03, 6.75) * mm, v(38.91, 6.64) * mm, v(38.91, 6.44) * mm]});
            skFitSpline(sketch, "E247", {"points": [v(38.91, 6.44) * mm, v(38.91, 6.36) * mm, v(38.92, 6.28) * mm, v(38.94, 6.21) * mm]});
            skFitSpline(sketch, "E248", {"points": [v(38.94, 6.21) * mm, v(38.96, 6.16) * mm, v(38.97, 6.1) * mm, v(38.97, 6) * mm]});
            skLineSegment(sketch, "E249", {"start": v(-10.02, -1.95) * mm, "end": v(-21.16, -0.6) * mm});
            skLineSegment(sketch, "E250", {"start": v(-21.16, -0.6) * mm, "end": v(-28.6, -9.01) * mm});
            skLineSegment(sketch, "E251", {"start": v(-28.6, -9.01) * mm, "end": v(-30.75, 2) * mm});
            skLineSegment(sketch, "E252", {"start": v(-30.75, 2) * mm, "end": v(-41.05, 6.46) * mm});
            skLineSegment(sketch, "E253", {"start": v(-41.05, 6.46) * mm, "end": v(-31.24, 11.92) * mm});
            skLineSegment(sketch, "E254", {"start": v(-31.24, 11.92) * mm, "end": v(-30.18, 23.1) * mm});
            skLineSegment(sketch, "E255", {"start": v(-30.18, 23.1) * mm, "end": v(-21.96, 15.45) * mm});
            skLineSegment(sketch, "E256", {"start": v(-21.96, 15.45) * mm, "end": v(-11, 17.9) * mm});
            skLineSegment(sketch, "E257", {"start": v(-11, 17.9) * mm, "end": v(-15.73, 7.71) * mm});
            skLineSegment(sketch, "E258", {"start": v(-15.73, 7.71) * mm, "end": v(-10.02, -1.95) * mm});
            skLineSegment(sketch, "E259", {"start": v(2.58, 4.64) * mm, "end": v(-1.36, 6.53) * mm});
            skLineSegment(sketch, "E260", {"start": v(-1.36, 6.53) * mm, "end": v(-5.15, 4.35) * mm});
            skLineSegment(sketch, "E261", {"start": v(-5.15, 4.35) * mm, "end": v(-4.57, 8.69) * mm});
            skLineSegment(sketch, "E262", {"start": v(-4.57, 8.69) * mm, "end": v(-7.81, 11.62) * mm});
            skLineSegment(sketch, "E263", {"start": v(-7.81, 11.62) * mm, "end": v(-3.51, 12.4) * mm});
            skLineSegment(sketch, "E264", {"start": v(-3.51, 12.4) * mm, "end": v(-1.72, 16.4) * mm});
            skLineSegment(sketch, "E265", {"start": v(-1.72, 16.4) * mm, "end": v(0.36, 12.55) * mm});
            skLineSegment(sketch, "E266", {"start": v(0.36, 12.55) * mm, "end": v(4.7, 12.08) * mm});
            skLineSegment(sketch, "E267", {"start": v(4.7, 12.08) * mm, "end": v(1.69, 8.92) * mm});
            skLineSegment(sketch, "E268", {"start": v(1.69, 8.92) * mm, "end": v(2.58, 4.64) * mm});
            skLineSegment(sketch, "E269.bottom", {"start": v(-46.5, 32.36) * mm, "end": v(46.5, 32.36) * mm});
            skLineSegment(sketch, "E269.top", {"start": v(-46.5, -32.36) * mm, "end": v(46.5, -32.36) * mm});
            skLineSegment(sketch, "E269.left", {"start": v(-46.5, 32.36) * mm, "end": v(-46.5, -32.36) * mm});
            skLineSegment(sketch, "E269.right", {"start": v(46.5, 32.36) * mm, "end": v(46.5, -32.36) * mm});
            skSolve(sketch);
        }
        {
            var Q0;
            {var subQ14=sQuery(id+"F0.wireOp",EDGE,"E10");Q0=makeQuery(id+"F0.imprint","IMPRINT",FACE,{"disambiguationData":[TD([[makeQuery(id+"F0.imprint","IMPRINT",EDGE,{"derivedFrom":subQ14}),1.0]])]});}
            var Q1;
            {var subQ4=sQuery(id+"F0.wireOp",EDGE,"E14");Q1=makeQuery(id+"F0.imprint","IMPRINT",FACE,{"disambiguationData":[TD([[makeQuery(id+"F0.imprint","IMPRINT",EDGE,{"derivedFrom":subQ4}),1.0]])]});}
            var Q2;
            {var subQ0=sQuery(id+"F0.wireOp",EDGE,"E41");Q2=makeQuery(id+"F0.imprint","IMPRINT",FACE,{"disambiguationData":[TD([[makeQuery(id+"F0.imprint","IMPRINT",EDGE,{"derivedFrom":subQ0}),1.0]])]});}
            var Q3;
            {var subQ10=sQuery(id+"F0.wireOp",EDGE,"E86");Q3=makeQuery(id+"F0.imprint","IMPRINT",FACE,{"disambiguationData":[TD([[makeQuery(id+"F0.imprint","IMPRINT",EDGE,{"derivedFrom":subQ10}),1.0]])]});}
            var Q4;
            {var subQ0=sQuery(id+"F0.wireOp",EDGE,"E103");Q4=makeQuery(id+"F0.imprint","IMPRINT",FACE,{"disambiguationData":[TD([[makeQuery(id+"F0.imprint","IMPRINT",EDGE,{"derivedFrom":subQ0}),1.0]])]});}
            var Q5;
            {var subQ5=sQuery(id+"F0.wireOp",EDGE,"E46");Q5=makeQuery(id+"F0.imprint","IMPRINT",FACE,{"disambiguationData":[TD([[makeQuery(id+"F0.imprint","IMPRINT",EDGE,{"derivedFrom":subQ5}),1.0]])]});}
            var Q6;
            Q6=makeQuery(id+"F0.imprint","IMPRINT",FACE,{"disambiguationData":[TD([[makeQuery(id+"F0.imprint","IMPRINT",EDGE,{"derivedFrom":sQuery(id+"F0.wireOp",EDGE,"E118")}),1.0]])]});
            var Q7;
            {var subQ5=sQuery(id+"F0.wireOp",EDGE,"E148");Q7=makeQuery(id+"F0.imprint","IMPRINT",FACE,{"disambiguationData":[TD([[makeQuery(id+"F0.imprint","IMPRINT",EDGE,{"derivedFrom":subQ5}),1.0]])]});}
            var Q8;
            Q8=makeQuery(id+"F0.imprint","IMPRINT",FACE,{"disambiguationData":[TD([[makeQuery(id+"F0.imprint","IMPRINT",EDGE,{"derivedFrom":sQuery(id+"F0.wireOp",EDGE,"E142")}),1.0]])]});
            var Q9;
            Q9=makeQuery(id+"F0.imprint","IMPRINT",FACE,{"disambiguationData":[TD([[makeQuery(id+"F0.imprint","IMPRINT",EDGE,{"derivedFrom":sQuery(id+"F0.wireOp",EDGE,"E195")}),1.0]])]});
            extrude(context, id + "F1", {"entities" : qUnion([Q0, Q1, Q2, Q3, Q4, Q5, Q6, Q7, Q8, Q9]), "depth" : 3 * mm, "offsetDistance" : 25 * mm});
        }
        {
            var Q0;
            Q0=makeQuery(id+"F0.imprint","IMPRINT",FACE,{"disambiguationData":[TD([[makeQuery(id+"F0.imprint","IMPRINT",EDGE,{"derivedFrom":sQuery(id+"F0.wireOp",EDGE,"E0")}),1.0]])]});
            var Q1;
            {var subQ8=sQuery(id+"F0.wireOp",EDGE,"E10");Q1=makeQuery(id+"F0.imprint","IMPRINT",FACE,{"disambiguationData":[TD([[makeQuery(id+"F0.imprint","IMPRINT",EDGE,{"derivedFrom":subQ8}),-1.0]])]});}
            var Q2;
            {var subQ0=sQuery(id+"F0.wireOp",EDGE,"E34");Q2=makeQuery(id+"F0.imprint","IMPRINT",FACE,{"disambiguationData":[TD([[makeQuery(id+"F0.imprint","IMPRINT",EDGE,{"derivedFrom":subQ0}),-1.0]])]});}
            var Q3;
            {var subQ14=sQuery(id+"F0.wireOp",EDGE,"E10");Q3=makeQuery(id+"F0.imprint","IMPRINT",FACE,{"disambiguationData":[TD([[makeQuery(id+"F0.imprint","IMPRINT",EDGE,{"derivedFrom":subQ14}),1.0]])]});}
            var Q4;
            {var subQ0=sQuery(id+"F0.wireOp",EDGE,"E103");Q4=makeQuery(id+"F0.imprint","IMPRINT",FACE,{"disambiguationData":[TD([[makeQuery(id+"F0.imprint","IMPRINT",EDGE,{"derivedFrom":subQ0}),1.0]])]});}
            var Q5;
            {var subQ5=sQuery(id+"F0.wireOp",EDGE,"E46");Q5=makeQuery(id+"F0.imprint","IMPRINT",FACE,{"disambiguationData":[TD([[makeQuery(id+"F0.imprint","IMPRINT",EDGE,{"derivedFrom":subQ5}),1.0]])]});}
            var Q6;
            Q6=makeQuery(id+"F0.imprint","IMPRINT",FACE,{"disambiguationData":[TD([[makeQuery(id+"F0.imprint","IMPRINT",EDGE,{"derivedFrom":sQuery(id+"F0.wireOp",EDGE,"E118")}),1.0]])]});
            var Q7;
            {var subQ5=sQuery(id+"F0.wireOp",EDGE,"E148");Q7=makeQuery(id+"F0.imprint","IMPRINT",FACE,{"disambiguationData":[TD([[makeQuery(id+"F0.imprint","IMPRINT",EDGE,{"derivedFrom":subQ5}),1.0]])]});}
            var Q8;
            Q8=makeQuery(id+"F0.imprint","IMPRINT",FACE,{"disambiguationData":[TD([[makeQuery(id+"F0.imprint","IMPRINT",EDGE,{"derivedFrom":sQuery(id+"F0.wireOp",EDGE,"E195")}),1.0]])]});
            extrude(context, id + "F2", {"entities" : qUnion([Q0, Q1, Q2, Q3, Q4, Q5, Q6, Q7, Q8]), "oppositeDirection" : true, "depth" : 3 * mm, "offsetDistance" : 25 * mm});
        }
        {
            var Q0;
            Q0=makeQuery(id+"F2.opExtrude","CAP_EDGE",EDGE,{"disambiguationData":[OSD([sQuery(id+"F0.wireOp",EDGE,"E269.left")])],"isStart":true});
            var Q1;
            Q1=makeQuery(id+"F2.opExtrude","CAP_EDGE",EDGE,{"disambiguationData":[OSD([sQuery(id+"F0.wireOp",EDGE,"E269.bottom")])],"isStart":true});
            var Q2;
            Q2=makeQuery(id+"F2.opExtrude","CAP_EDGE",EDGE,{"disambiguationData":[OSD([sQuery(id+"F0.wireOp",EDGE,"E269.right")])],"isStart":true});
            var Q3;
            Q3=makeQuery(id+"F2.opExtrude","CAP_EDGE",EDGE,{"disambiguationData":[OSD([sQuery(id+"F0.wireOp",EDGE,"E269.top")])],"isStart":true});
            chamfer(context, id + "F3", {"entities" : qUnion([Q0, Q1, Q2, Q3]), "width" : 1 * mm, "tangentPropagation" : true});
        }
    });
